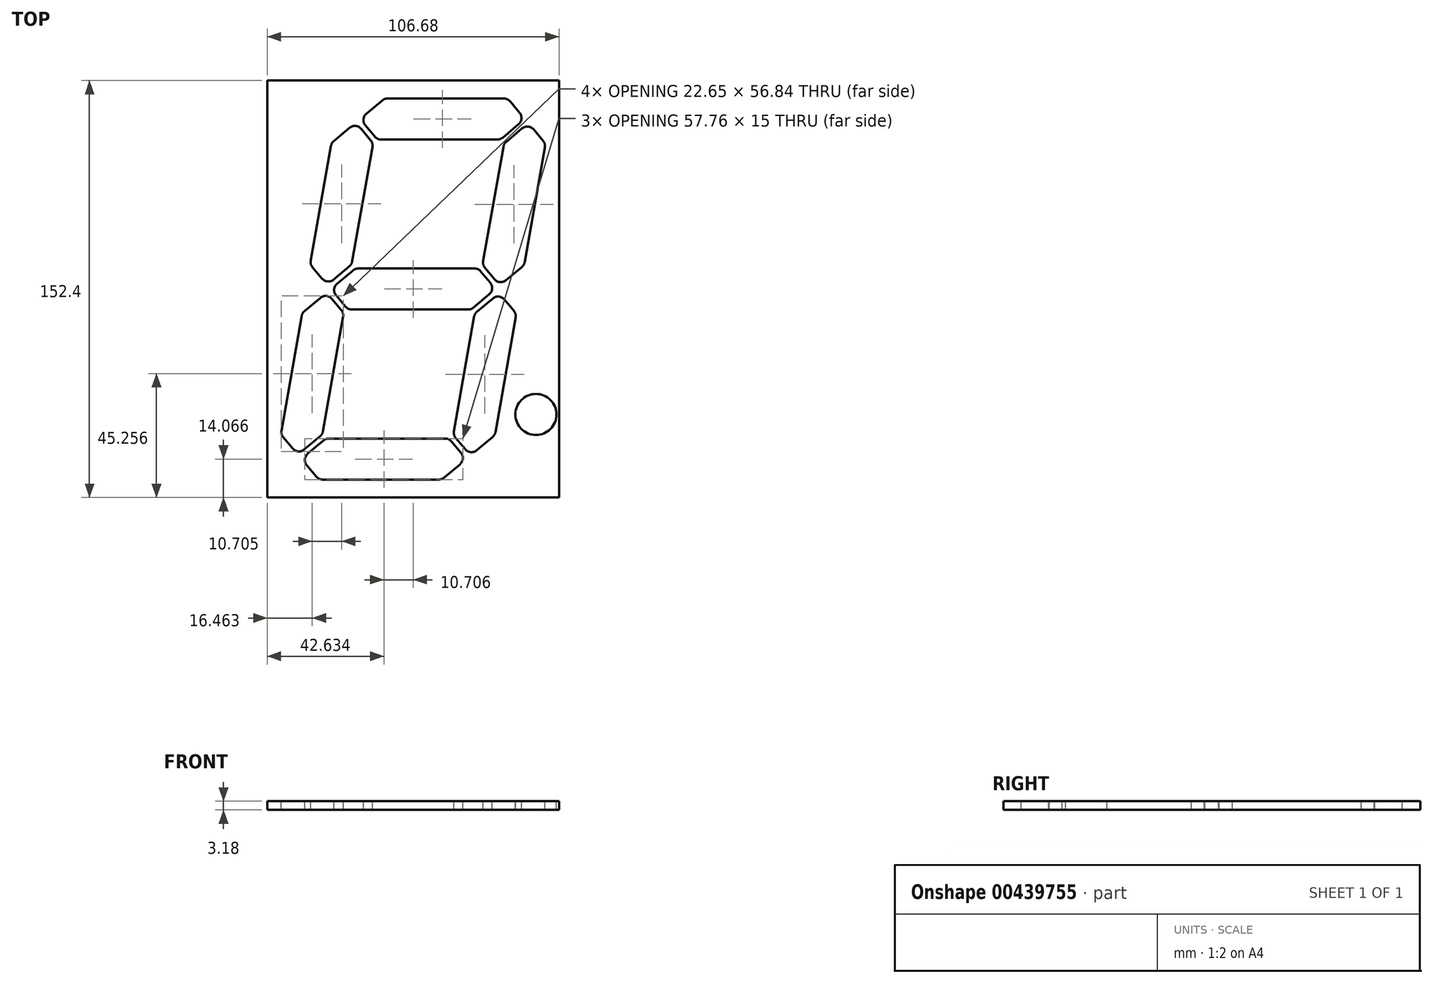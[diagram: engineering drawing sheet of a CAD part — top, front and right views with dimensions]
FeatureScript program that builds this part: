
annotation { "Feature Type Name" : "Feature", "Feature Type Description" : "" }
export const myFeature = defineFeature(function(context is Context, id is Id, definition is map)
    precondition{}
    {
        {
            var Q0;
            Q0=qCreatedBy(makeId("Top.planeOp"),FACE);
            var sketch = newSketch(context, id + "F0", { "sketchPlane" : qUnion([Q0])});
            skLineSegment(sketch, "E0.bottom", {"start": v(-53.34, 76.2) * mm, "end": v(53.34, 76.2) * mm});
            skLineSegment(sketch, "E0.top", {"start": v(-53.34, -76.2) * mm, "end": v(53.34, -76.2) * mm});
            skLineSegment(sketch, "E0.left", {"start": v(-53.34, 76.2) * mm, "end": v(-53.34, -76.2) * mm});
            skLineSegment(sketch, "E0.right", {"start": v(53.34, 76.2) * mm, "end": v(53.34, -76.2) * mm});
            skLineSegment(sketch, "E1", {"start": v(-53.34, 0) * mm, "end": v(0, 0) * mm, "construction": true});
            skLineSegment(sketch, "E2", {"start": v(0, 0) * mm, "end": v(53.34, 0) * mm, "construction": true});
            skLineSegment(sketch, "E3", {"start": v(0, 76.2) * mm, "end": v(0, 0) * mm, "construction": true});
            skLineSegment(sketch, "E4", {"start": v(0, -76.2) * mm, "end": v(0, 0) * mm, "construction": true});
            skSolve(sketch);
        }
        {
            var Q0;
            Q0=qSketchRegion(id+"F0",true);
            extrude(context, id + "F1", {"entities" : qUnion([Q0]), "depth" : 3.17 * mm});
        }
        {
            var Q0;
            Q0=makeQuery(id+"F1.opExtrude","CAP_FACE",FACE,{"disambiguationData":[OSD([sQuery(id+"F0.wireOp",EDGE,"E0.bottom"),sQuery(id+"F0.wireOp",EDGE,"E0.top"),sQuery(id+"F0.wireOp",EDGE,"E0.left"),sQuery(id+"F0.wireOp",EDGE,"E0.right")])],"isStart":false});
            var sketch = newSketch(context, id + "F2", { "sketchPlane" : qUnion([Q0])});
            skLineSegment(sketch, "E5", {"start": v(-38.52, -60.2) * mm, "end": v(-32.72, -55.34) * mm});
            skLineSegment(sketch, "E6", {"start": v(-30.8, -54.63) * mm, "end": v(11.72, -54.63) * mm});
            skLineSegment(sketch, "E7", {"start": v(14.02, -55.7) * mm, "end": v(17.48, -59.84) * mm});
            skLineSegment(sketch, "E8", {"start": v(17.11, -64.06) * mm, "end": v(11.3, -68.93) * mm});
            skLineSegment(sketch, "E9", {"start": v(9.38, -69.63) * mm, "end": v(-33.13, -69.63) * mm});
            skLineSegment(sketch, "E10", {"start": v(-35.43, -68.56) * mm, "end": v(-38.9, -64.43) * mm});
            skLineSegment(sketch, "E11", {"start": v(-39.8, -58.67) * mm, "end": v(-34, -53.8) * mm});
            skLineSegment(sketch, "E12", {"start": v(-32.98, -52.03) * mm, "end": v(-25.6, -10.16) * mm});
            skLineSegment(sketch, "E13", {"start": v(-26.25, -7.71) * mm, "end": v(-29.72, -3.58) * mm});
            skLineSegment(sketch, "E14", {"start": v(-33.95, -3.21) * mm, "end": v(-39.75, -8.08) * mm});
            skLineSegment(sketch, "E15", {"start": v(-40.78, -9.86) * mm, "end": v(-48.16, -51.72) * mm});
            skLineSegment(sketch, "E16", {"start": v(-47.5, -54.17) * mm, "end": v(-44.04, -58.3) * mm});
            skLineSegment(sketch, "E17", {"start": v(15.55, -54.42) * mm, "end": v(19.01, -58.55) * mm});
            skLineSegment(sketch, "E18", {"start": v(23.24, -58.92) * mm, "end": v(29.04, -54.05) * mm});
            skLineSegment(sketch, "E19", {"start": v(30.07, -52.27) * mm, "end": v(37.45, -10.4) * mm});
            skLineSegment(sketch, "E20", {"start": v(36.8, -7.96) * mm, "end": v(33.33, -3.83) * mm});
            skLineSegment(sketch, "E21", {"start": v(29.1, -3.46) * mm, "end": v(23.3, -8.33) * mm});
            skLineSegment(sketch, "E22", {"start": v(22.27, -10.1) * mm, "end": v(14.9, -51.97) * mm});
            skLineSegment(sketch, "E23", {"start": v(-40.82, -62.13) * mm, "end": v(19.41, -62.13) * mm, "construction": true});
            skLineSegment(sketch, "E24", {"start": v(-42.1, -60.6) * mm, "end": v(-31.65, -1.29) * mm, "construction": true});
            skLineSegment(sketch, "E25", {"start": v(31.4, -1.53) * mm, "end": v(20.94, -60.85) * mm, "construction": true});
            skLineSegment(sketch, "E26", {"start": v(-33.17, -53.1) * mm, "end": v(-47.94, -50.5) * mm, "construction": true});
            skLineSegment(sketch, "E27", {"start": v(29.88, -53.35) * mm, "end": v(15.1, -50.74) * mm, "construction": true});
            skLineSegment(sketch, "E28", {"start": v(-31.88, -54.63) * mm, "end": v(-31.88, -69.63) * mm, "construction": true});
            skLineSegment(sketch, "E29", {"start": v(-28.19, -2.3) * mm, "end": v(-24.72, -6.43) * mm});
            skLineSegment(sketch, "E30", {"start": v(-22.42, -7.5) * mm, "end": v(20.09, -7.5) * mm});
            skLineSegment(sketch, "E31", {"start": v(22.01, -6.8) * mm, "end": v(27.82, -1.93) * mm});
            skLineSegment(sketch, "E32", {"start": v(28.19, 2.3) * mm, "end": v(24.72, 6.43) * mm});
            skLineSegment(sketch, "E33", {"start": v(22.42, 7.5) * mm, "end": v(-20.09, 7.5) * mm});
            skLineSegment(sketch, "E34", {"start": v(-22.01, 6.8) * mm, "end": v(-27.82, 1.93) * mm});
            skLineSegment(sketch, "E35", {"start": v(-30.12, 0) * mm, "end": v(30.12, 0) * mm, "construction": true});
            skLineSegment(sketch, "E36", {"start": v(-21.18, 7.5) * mm, "end": v(-21.18, -7.5) * mm, "construction": true});
            skLineSegment(sketch, "E37", {"start": v(19.41, -62.13) * mm, "end": v(20.94, -60.85) * mm, "construction": true});
            skLineSegment(sketch, "E38", {"start": v(-42.1, -60.6) * mm, "end": v(-40.82, -62.13) * mm, "construction": true});
            skLineSegment(sketch, "E39", {"start": v(-25.35, -8.79) * mm, "end": v(-23.82, -7.5) * mm, "construction": true});
            skLineSegment(sketch, "E40", {"start": v(21.18, -7.5) * mm, "end": v(22.46, -9.03) * mm, "construction": true});
            skLineSegment(sketch, "E41", {"start": v(-29.1, 3.46) * mm, "end": v(-23.3, 8.33) * mm});
            skLineSegment(sketch, "E42", {"start": v(-22.27, 10.1) * mm, "end": v(-14.9, 51.97) * mm});
            skLineSegment(sketch, "E43", {"start": v(-15.55, 54.42) * mm, "end": v(-19.01, 58.55) * mm});
            skLineSegment(sketch, "E44", {"start": v(-23.24, 58.92) * mm, "end": v(-29.04, 54.05) * mm});
            skLineSegment(sketch, "E45", {"start": v(-30.07, 52.27) * mm, "end": v(-37.45, 10.4) * mm});
            skLineSegment(sketch, "E46", {"start": v(-36.8, 7.96) * mm, "end": v(-33.33, 3.83) * mm});
            skLineSegment(sketch, "E47", {"start": v(-31.4, 1.53) * mm, "end": v(-20.94, 60.85) * mm, "construction": true});
            skLineSegment(sketch, "E48", {"start": v(-22.46, 9.03) * mm, "end": v(-37.24, 11.64) * mm, "construction": true});
            skLineSegment(sketch, "E49", {"start": v(-22.46, 9.03) * mm, "end": v(-21.18, 7.5) * mm, "construction": true});
            skLineSegment(sketch, "E50", {"start": v(26.25, 7.71) * mm, "end": v(29.72, 3.58) * mm});
            skLineSegment(sketch, "E51", {"start": v(33.95, 3.21) * mm, "end": v(39.75, 8.08) * mm});
            skLineSegment(sketch, "E52", {"start": v(40.78, 9.86) * mm, "end": v(48.16, 51.72) * mm});
            skLineSegment(sketch, "E53", {"start": v(47.5, 54.17) * mm, "end": v(44.04, 58.3) * mm});
            skLineSegment(sketch, "E54", {"start": v(39.8, 58.67) * mm, "end": v(34, 53.8) * mm});
            skLineSegment(sketch, "E55", {"start": v(32.98, 52.03) * mm, "end": v(25.6, 10.16) * mm});
            skLineSegment(sketch, "E56", {"start": v(31.65, 1.29) * mm, "end": v(42.1, 60.6) * mm, "construction": true});
            skLineSegment(sketch, "E57", {"start": v(40.59, 8.79) * mm, "end": v(25.81, 11.4) * mm, "construction": true});
            skLineSegment(sketch, "E58", {"start": v(23.82, 7.5) * mm, "end": v(25.35, 8.79) * mm, "construction": true});
            skLineSegment(sketch, "E59", {"start": v(-17.48, 59.84) * mm, "end": v(-14.02, 55.7) * mm});
            skLineSegment(sketch, "E60", {"start": v(-11.72, 54.63) * mm, "end": v(30.8, 54.63) * mm});
            skLineSegment(sketch, "E61", {"start": v(32.72, 55.34) * mm, "end": v(38.52, 60.2) * mm});
            skLineSegment(sketch, "E62", {"start": v(38.9, 64.43) * mm, "end": v(35.43, 68.56) * mm});
            skLineSegment(sketch, "E63", {"start": v(33.13, 69.63) * mm, "end": v(-9.38, 69.63) * mm});
            skLineSegment(sketch, "E64", {"start": v(-11.3, 68.93) * mm, "end": v(-17.11, 64.06) * mm});
            skLineSegment(sketch, "E65", {"start": v(-19.41, 62.13) * mm, "end": v(40.82, 62.13) * mm, "construction": true});
            skLineSegment(sketch, "E66", {"start": v(-10.47, 69.63) * mm, "end": v(-10.47, 54.63) * mm, "construction": true});
            skLineSegment(sketch, "E67", {"start": v(-14.65, 53.35) * mm, "end": v(-13.12, 54.63) * mm, "construction": true});
            skLineSegment(sketch, "E68", {"start": v(31.88, 54.63) * mm, "end": v(33.17, 53.1) * mm, "construction": true});
            skLineSegment(sketch, "E69", {"start": v(34.53, 69.63) * mm, "end": v(34.53, 76.2) * mm, "construction": true});
            skLineSegment(sketch, "E70", {"start": v(-34.53, -69.63) * mm, "end": v(-34.53, -76.2) * mm, "construction": true});
            skLineSegment(sketch, "E71", {"start": v(-48.4, -53.1) * mm, "end": v(-53.34, -53.1) * mm, "construction": true});
            skLineSegment(sketch, "E72", {"start": v(48.4, 53.1) * mm, "end": v(53.34, 53.1) * mm, "construction": true});
            skCircle(sketch, "E73", {"center": v(44.88, -45.85) * mm, "radius": 7.5 * mm});
            skLineSegment(sketch, "E74", {"start": v(29.88, -53.35) * mm, "end": v(44.88, -53.35) * mm, "construction": true});
            skLineSegment(sketch, "E75", {"start": v(44.88, -38.35) * mm, "end": v(44.88, -53.35) * mm, "construction": true});
            skPoint(sketch, "E76.visualSharp", {"position": v(-40.82, -62.13) * mm});
            skArc(sketch, "E76.filletArc", {"start": v(-38.52, -60.2) * mm, "mid": v(-39.58, -62.24) * mm, "end": v(-38.9, -64.43) * mm});
            skPoint(sketch, "E77.visualSharp", {"position": v(-34.53, -69.63) * mm});
            skArc(sketch, "E77.filletArc", {"start": v(-35.43, -68.56) * mm, "mid": v(-34.4, -69.35) * mm, "end": v(-33.13, -69.63) * mm});
            skPoint(sketch, "E78.visualSharp", {"position": v(-31.88, -54.63) * mm});
            skArc(sketch, "E78.filletArc", {"start": v(-30.8, -54.63) * mm, "mid": v(-31.82, -54.81) * mm, "end": v(-32.72, -55.34) * mm});
            skPoint(sketch, "E79.visualSharp", {"position": v(13.12, -54.63) * mm});
            skArc(sketch, "E79.filletArc", {"start": v(14.02, -55.7) * mm, "mid": v(12.99, -54.92) * mm, "end": v(11.72, -54.63) * mm});
            skPoint(sketch, "E80.visualSharp", {"position": v(10.47, -69.63) * mm});
            skArc(sketch, "E80.filletArc", {"start": v(9.38, -69.63) * mm, "mid": v(10.4, -69.45) * mm, "end": v(11.3, -68.93) * mm});
            skPoint(sketch, "E81.visualSharp", {"position": v(19.41, -62.13) * mm});
            skArc(sketch, "E81.filletArc", {"start": v(17.11, -64.06) * mm, "mid": v(18.17, -62.03) * mm, "end": v(17.48, -59.84) * mm});
            skPoint(sketch, "E82.visualSharp", {"position": v(20.94, -60.85) * mm});
            skArc(sketch, "E82.filletArc", {"start": v(19.01, -58.55) * mm, "mid": v(21.05, -59.61) * mm, "end": v(23.24, -58.92) * mm});
            skPoint(sketch, "E83.visualSharp", {"position": v(14.65, -53.35) * mm});
            skArc(sketch, "E83.filletArc", {"start": v(14.9, -51.97) * mm, "mid": v(14.95, -53.27) * mm, "end": v(15.55, -54.42) * mm});
            skPoint(sketch, "E84.visualSharp", {"position": v(29.88, -53.35) * mm});
            skArc(sketch, "E84.filletArc", {"start": v(29.04, -54.05) * mm, "mid": v(29.71, -53.25) * mm, "end": v(30.07, -52.27) * mm});
            skPoint(sketch, "E85.visualSharp", {"position": v(-42.1, -60.6) * mm});
            skArc(sketch, "E85.filletArc", {"start": v(-44.04, -58.3) * mm, "mid": v(-42, -59.36) * mm, "end": v(-39.8, -58.67) * mm});
            skPoint(sketch, "E86.visualSharp", {"position": v(-33.17, -53.1) * mm});
            skArc(sketch, "E86.filletArc", {"start": v(-34, -53.8) * mm, "mid": v(-33.34, -53) * mm, "end": v(-32.98, -52.03) * mm});
            skPoint(sketch, "E87.visualSharp", {"position": v(-48.4, -53.1) * mm});
            skArc(sketch, "E87.filletArc", {"start": v(-48.16, -51.72) * mm, "mid": v(-48.1, -53.02) * mm, "end": v(-47.5, -54.17) * mm});
            skPoint(sketch, "E88.visualSharp", {"position": v(-40.59, -8.79) * mm});
            skArc(sketch, "E88.filletArc", {"start": v(-39.75, -8.08) * mm, "mid": v(-40.42, -8.88) * mm, "end": v(-40.78, -9.86) * mm});
            skPoint(sketch, "E89.visualSharp", {"position": v(-31.65, -1.29) * mm});
            skArc(sketch, "E89.filletArc", {"start": v(-29.72, -3.58) * mm, "mid": v(-31.76, -2.52) * mm, "end": v(-33.95, -3.21) * mm});
            skPoint(sketch, "E90.visualSharp", {"position": v(-25.35, -8.79) * mm});
            skArc(sketch, "E90.filletArc", {"start": v(-25.6, -10.16) * mm, "mid": v(-25.65, -8.87) * mm, "end": v(-26.25, -7.71) * mm});
            skPoint(sketch, "E91.visualSharp", {"position": v(-23.82, -7.5) * mm});
            skArc(sketch, "E91.filletArc", {"start": v(-24.72, -6.43) * mm, "mid": v(-23.7, -7.22) * mm, "end": v(-22.42, -7.5) * mm});
            skPoint(sketch, "E92.visualSharp", {"position": v(-30.12, 0) * mm});
            skArc(sketch, "E92.filletArc", {"start": v(-27.82, 1.93) * mm, "mid": v(-28.88, -0.1) * mm, "end": v(-28.19, -2.3) * mm});
            skPoint(sketch, "E93.visualSharp", {"position": v(-21.18, 7.5) * mm});
            skArc(sketch, "E93.filletArc", {"start": v(-20.09, 7.5) * mm, "mid": v(-21.11, 7.32) * mm, "end": v(-22.01, 6.8) * mm});
            skPoint(sketch, "E94.visualSharp", {"position": v(23.82, 7.5) * mm});
            skArc(sketch, "E94.filletArc", {"start": v(24.72, 6.43) * mm, "mid": v(23.7, 7.22) * mm, "end": v(22.42, 7.5) * mm});
            skPoint(sketch, "E95.visualSharp", {"position": v(30.12, 0) * mm});
            skArc(sketch, "E95.filletArc", {"start": v(27.82, -1.93) * mm, "mid": v(28.88, 0.1) * mm, "end": v(28.19, 2.3) * mm});
            skPoint(sketch, "E96.visualSharp", {"position": v(21.18, -7.5) * mm});
            skArc(sketch, "E96.filletArc", {"start": v(20.09, -7.5) * mm, "mid": v(21.11, -7.32) * mm, "end": v(22.01, -6.8) * mm});
            skPoint(sketch, "E97.visualSharp", {"position": v(22.46, -9.03) * mm});
            skArc(sketch, "E97.filletArc", {"start": v(23.3, -8.33) * mm, "mid": v(22.63, -9.13) * mm, "end": v(22.27, -10.1) * mm});
            skPoint(sketch, "E98.visualSharp", {"position": v(31.4, -1.53) * mm});
            skArc(sketch, "E98.filletArc", {"start": v(33.33, -3.83) * mm, "mid": v(31.3, -2.77) * mm, "end": v(29.1, -3.46) * mm});
            skPoint(sketch, "E99.visualSharp", {"position": v(37.7, -9.03) * mm});
            skArc(sketch, "E99.filletArc", {"start": v(37.45, -10.4) * mm, "mid": v(37.4, -9.11) * mm, "end": v(36.8, -7.96) * mm});
            skPoint(sketch, "E100.visualSharp", {"position": v(31.65, 1.29) * mm});
            skArc(sketch, "E100.filletArc", {"start": v(29.72, 3.58) * mm, "mid": v(31.76, 2.52) * mm, "end": v(33.95, 3.21) * mm});
            skPoint(sketch, "E101.visualSharp", {"position": v(40.59, 8.79) * mm});
            skArc(sketch, "E101.filletArc", {"start": v(39.75, 8.08) * mm, "mid": v(40.42, 8.88) * mm, "end": v(40.78, 9.86) * mm});
            skPoint(sketch, "E102.visualSharp", {"position": v(25.35, 8.79) * mm});
            skArc(sketch, "E102.filletArc", {"start": v(25.6, 10.16) * mm, "mid": v(25.65, 8.87) * mm, "end": v(26.25, 7.71) * mm});
            skPoint(sketch, "E103.visualSharp", {"position": v(-22.46, 9.03) * mm});
            skArc(sketch, "E103.filletArc", {"start": v(-23.3, 8.33) * mm, "mid": v(-22.63, 9.13) * mm, "end": v(-22.27, 10.1) * mm});
            skPoint(sketch, "E104.visualSharp", {"position": v(-31.4, 1.53) * mm});
            skArc(sketch, "E104.filletArc", {"start": v(-33.33, 3.83) * mm, "mid": v(-31.3, 2.77) * mm, "end": v(-29.1, 3.46) * mm});
            skPoint(sketch, "E105.visualSharp", {"position": v(-37.7, 9.03) * mm});
            skArc(sketch, "E105.filletArc", {"start": v(-37.45, 10.4) * mm, "mid": v(-37.4, 9.11) * mm, "end": v(-36.8, 7.96) * mm});
            skPoint(sketch, "E106.visualSharp", {"position": v(-29.88, 53.35) * mm});
            skArc(sketch, "E106.filletArc", {"start": v(-29.04, 54.05) * mm, "mid": v(-29.71, 53.25) * mm, "end": v(-30.07, 52.27) * mm});
            skPoint(sketch, "E107.visualSharp", {"position": v(-20.94, 60.85) * mm});
            skArc(sketch, "E107.filletArc", {"start": v(-19.01, 58.55) * mm, "mid": v(-21.05, 59.61) * mm, "end": v(-23.24, 58.92) * mm});
            skPoint(sketch, "E108.visualSharp", {"position": v(-14.65, 53.35) * mm});
            skArc(sketch, "E108.filletArc", {"start": v(-14.9, 51.97) * mm, "mid": v(-14.95, 53.27) * mm, "end": v(-15.55, 54.42) * mm});
            skPoint(sketch, "E109.visualSharp", {"position": v(-13.12, 54.63) * mm});
            skArc(sketch, "E109.filletArc", {"start": v(-14.02, 55.7) * mm, "mid": v(-12.99, 54.92) * mm, "end": v(-11.72, 54.63) * mm});
            skPoint(sketch, "E110.visualSharp", {"position": v(-19.41, 62.13) * mm});
            skArc(sketch, "E110.filletArc", {"start": v(-17.11, 64.06) * mm, "mid": v(-18.17, 62.03) * mm, "end": v(-17.48, 59.84) * mm});
            skPoint(sketch, "E111.visualSharp", {"position": v(-10.47, 69.63) * mm});
            skArc(sketch, "E111.filletArc", {"start": v(-9.38, 69.63) * mm, "mid": v(-10.4, 69.45) * mm, "end": v(-11.3, 68.93) * mm});
            skPoint(sketch, "E112.visualSharp", {"position": v(34.53, 69.63) * mm});
            skArc(sketch, "E112.filletArc", {"start": v(35.43, 68.56) * mm, "mid": v(34.4, 69.35) * mm, "end": v(33.13, 69.63) * mm});
            skPoint(sketch, "E113.visualSharp", {"position": v(31.88, 54.63) * mm});
            skArc(sketch, "E113.filletArc", {"start": v(30.8, 54.63) * mm, "mid": v(31.82, 54.81) * mm, "end": v(32.72, 55.34) * mm});
            skPoint(sketch, "E114.visualSharp", {"position": v(40.82, 62.13) * mm});
            skArc(sketch, "E114.filletArc", {"start": v(38.52, 60.2) * mm, "mid": v(39.58, 62.24) * mm, "end": v(38.9, 64.43) * mm});
            skPoint(sketch, "E115.visualSharp", {"position": v(42.1, 60.6) * mm});
            skArc(sketch, "E115.filletArc", {"start": v(44.04, 58.3) * mm, "mid": v(42, 59.36) * mm, "end": v(39.8, 58.67) * mm});
            skPoint(sketch, "E116.visualSharp", {"position": v(33.17, 53.1) * mm});
            skArc(sketch, "E116.filletArc", {"start": v(34, 53.8) * mm, "mid": v(33.34, 53) * mm, "end": v(32.98, 52.03) * mm});
            skPoint(sketch, "E117.visualSharp", {"position": v(48.4, 53.1) * mm});
            skArc(sketch, "E117.filletArc", {"start": v(48.16, 51.72) * mm, "mid": v(48.1, 53.02) * mm, "end": v(47.5, 54.17) * mm});
            skSolve(sketch);
        }
        {
            var Q0;
            Q0=qSketchRegion(id+"F2",true);
            extrude(context, id + "F3", {"entities" : qUnion([Q0]), "operationType" : NewBodyOperationType.REMOVE, "endBound" : BoundingType.THROUGH_ALL, "oppositeDirection" : true, "depth" : 25.4 * mm});
        }
    });
